# Revit family: Trellis_Canopy-McD
name_source: partatom
category: Generic Models
revit_build: Autodesk Revit Architecture 2012 (Build: 20110309_2315(x64)
units: mm (PartAtom-declared; Revit-internal decimal feet)

## types (5) — shared parameters
Assembly Code = B2010400
Custom Support Left Offset = 0' - 0"
Fascia Finish = Metal - Aluminum - McD Yellow - McD
Fascia Height = 1' - 4"
Height = 0' - 8"
Keynote = 05.70.00
MasterFormat Number = 05.70.00
Panel Option = Yes
Support Width = 0' - 1"
Tieback Option = Yes

## per-type parameters (varying)
| type | Custom Tieback Height | Depth | Fascia Option | Length | Light Option | Standard Support Left Offset | Support Array | Support Depth | Support Left Offset | Support Spacing | Tieback Height | Trellis Fascia Linear Feet | Trellis Panel Area | Trellis Tube Linear Feet | Type Mark | Welcome Sign Height | Welcome Sign Option |
| Canopy - 8'-0" x 3'-0" | 0' - 0" | 3' - 0" | Yes | 8' - 0" | Yes | 1' - 0" | 2 | 2' - 8" | 1' - 0" | 6' - 0" | 2' - 1" | 14' - 0" | 18.76 SF | 26' - 8" | C1 | 1' - 4" | No |
| Canopy - 28'-0" x 3'-0" | 0' - 0" | 3' - 0" | Yes | 28' - 0" | Yes | 2' - 7 1/2" | 4 | 2' - 8" | 2' - 7 1/2" | 7' - 7" | 2' - 1" | 34' - 0" | 69.12 SF | 72' - 0" | C1 | 1' - 4" | Yes |
| Trellis - 6'-0" x 4'-0" | 2' - 1" | 4' - 0" | No | 6' - 0" | No | 1' - 0" | 2 | 3' - 8" | 1' - 0" | 4' - 0" | 2' - 1" | 0' - 0" | 18.97 SF | 26' - 8" | T1 | 0' - 8" | Yes |
| Trellis - 58'-8" x 4'-0" | 2' - 11" | 4' - 0" | No | 58' - 8" | No | 3' - 8" | 8 | 3' - 8" | 3' - 8" | 7' - 4" | 2' - 11" | 0' - 0" | 202.92 SF | 154' - 0" | T1 | 0' - 8" | Yes |
| Trellis - 15'-0" x 4'-0" | 2' - 11" | 4' - 0" | No | 15' - 0" | No | 3' - 10" | 2 | 3' - 8" | 3' - 10" | 7' - 4" | 2' - 11" | 0' - 0" | 51.03 SF | 44' - 8" | T1 | 0' - 8" | No |

## geometry (parser evidence)
native form markers: Sweep x11
no freeform markers — native parametric forms only
